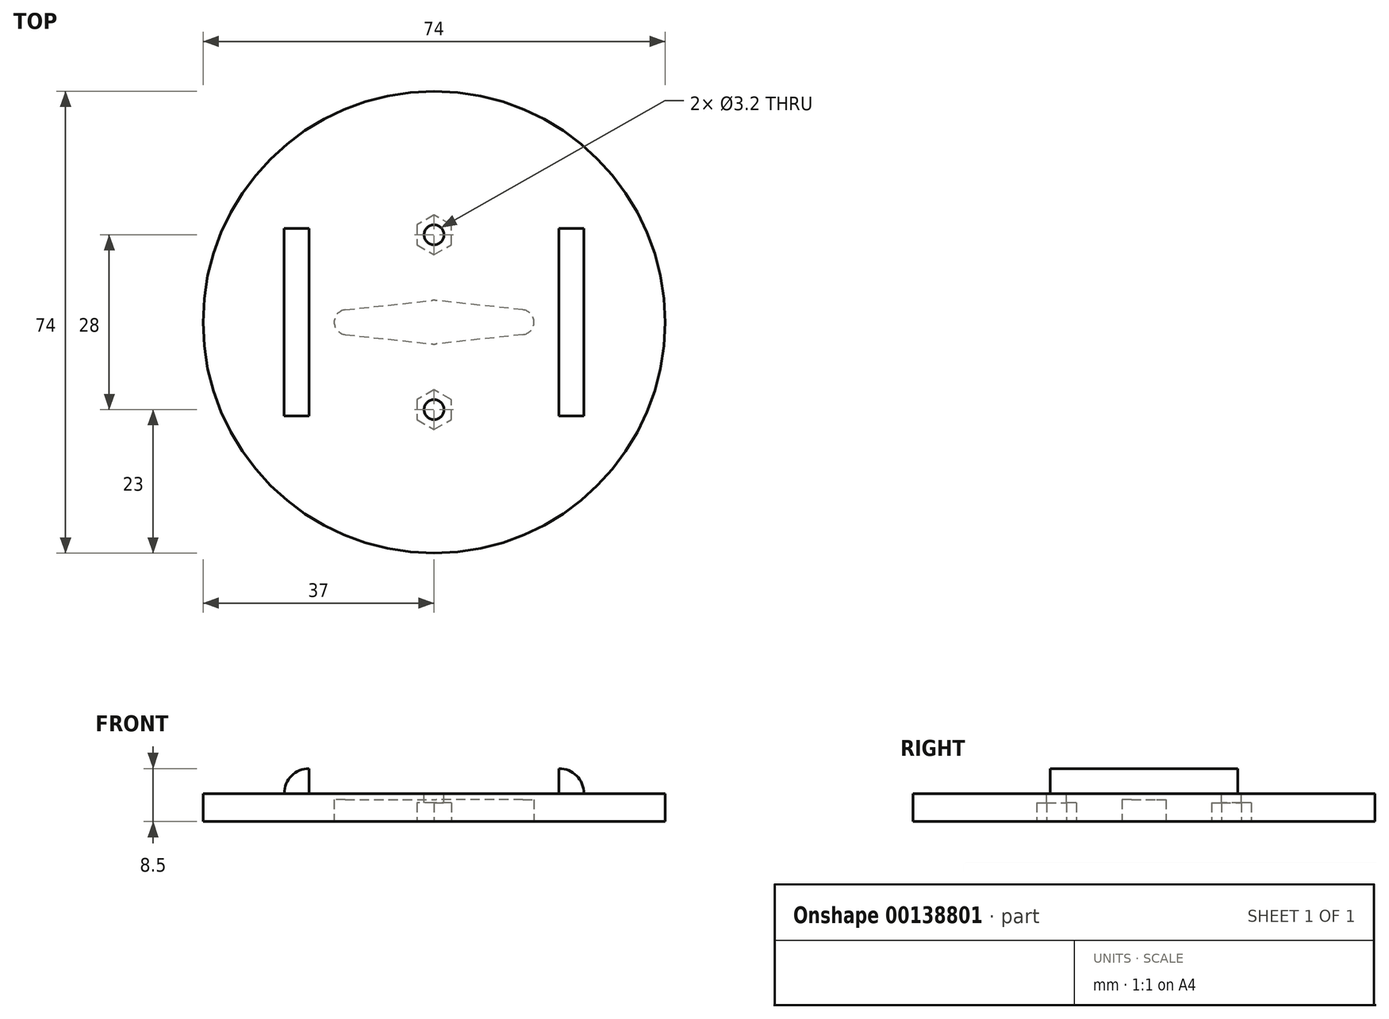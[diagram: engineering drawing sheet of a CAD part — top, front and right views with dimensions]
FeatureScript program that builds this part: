
annotation { "Feature Type Name" : "Feature", "Feature Type Description" : "" }
export const myFeature = defineFeature(function(context is Context, id is Id, definition is map)
    precondition{}
    {
        {
            var Q0;
            Q0=qCreatedBy(makeId("Top.planeOp"),FACE);
            var sketch = newSketch(context, id + "F0", { "sketchPlane" : qUnion([Q0])});
            skCircle(sketch, "E0", {"center": v(0, 0) * mm, "radius": 37 * mm});
            skSolve(sketch);
        }
        {
            var Q0;
            Q0=makeQuery(id+"F0.imprint","IMPRINT",FACE,{"disambiguationData":[TD([[makeQuery(id+"F0.imprint","IMPRINT",EDGE,{"derivedFrom":sQuery(id+"F0.wireOp",EDGE,"E0")}),1.0]])]});
            extrude(context, id + "F1", {"entities" : qUnion([Q0]), "depth" : 4.5 * mm});
        }
        {
            var Q0;
            Q0=makeQuery(id+"F1.opExtrude","CAP_FACE",FACE,{"disambiguationData":[OSD([sQuery(id+"F0.wireOp",EDGE,"E0")])],"isStart":true});
            var sketch = newSketch(context, id + "F2", { "sketchPlane" : qUnion([Q0])});
            skCircle(sketch, "E1", {"center": v(0, 0) * mm, "radius": 3.5 * mm});
            skLineSegment(sketch, "E2", {"start": v(0, 0) * mm, "end": v(0, 14) * mm});
            skCircle(sketch, "E3", {"center": v(0, 14) * mm, "radius": 2 * mm});
            skCircle(sketch, "E4.MirrorC", {"center": v(0, -14) * mm, "radius": 2 * mm});
            skLineSegment(sketch, "E5", {"start": v(-1.99, 14.21) * mm, "end": v(-3.48, 0.38) * mm});
            skLineSegment(sketch, "E6", {"start": v(1.99, 14.21) * mm, "end": v(3.48, 0.37) * mm});
            skLineSegment(sketch, "E7.MirrorCS", {"start": v(-1.99, -14.21) * mm, "end": v(-3.48, -0.38) * mm});
            skLineSegment(sketch, "E8.MirrorCS", {"start": v(1.99, -14.21) * mm, "end": v(3.48, -0.37) * mm});
            skSolve(sketch);
        }
        {
            var Q0;
            Q0=qSketchRegion(id+"F2",true);
            extrude(context, id + "F3", {"entities" : qUnion([Q0]), "operationType" : NewBodyOperationType.REMOVE, "oppositeDirection" : true, "depth" : 3.5 * mm});
        }
        {
            var Q0;
            Q0=qCreatedBy(makeId("Right.planeOp"),FACE);
            var sketch = newSketch(context, id + "F4", { "sketchPlane" : qUnion([Q0])});
            skLineSegment(sketch, "E9.0", {"start": v(-37, 4.5) * mm, "end": v(37, 4.5) * mm});
            skLineSegment(sketch, "E10", {"start": v(20, 4.5) * mm, "end": v(20, 8.5) * mm});
            skArc(sketch, "E11", {"start": v(20, 8.5) * mm, "mid": v(22.83, 7.33) * mm, "end": v(24, 4.5) * mm});
            skLineSegment(sketch, "E12.MirrorCS", {"start": v(-20, 4.5) * mm, "end": v(-20, 8.5) * mm});
            skArc(sketch, "E13.MirrorCS", {"start": v(-20, 8.5) * mm, "mid": v(-22.83, 7.33) * mm, "end": v(-24, 4.5) * mm});
            skSolve(sketch);
        }
        {
            var Q0;
            {var subQ0=sQuery(id+"F4.wireOp",EDGE,"E12.MirrorCS");Q0=makeQuery(id+"F4.imprint","IMPRINT",FACE,{"disambiguationData":[TD([[makeQuery(id+"F4.imprint","IMPRINT",EDGE,{"derivedFrom":subQ0}),1.0]])]});}
            var Q1;
            {var subQ0=sQuery(id+"F4.wireOp",EDGE,"E10");Q1=makeQuery(id+"F4.imprint","IMPRINT",FACE,{"disambiguationData":[TD([[makeQuery(id+"F4.imprint","IMPRINT",EDGE,{"derivedFrom":subQ0}),-1.0]])]});}
            extrude(context, id + "F5", {"entities" : qUnion([Q0, Q1]), "operationType" : NewBodyOperationType.ADD, "endBound" : BoundingType.SYMMETRIC, "depth" : 30 * mm});
        }
        {
            var Q0;
            Q0=makeQuery(id+"F1.opExtrude","CAP_FACE",FACE,{"disambiguationData":[OSD([sQuery(id+"F0.wireOp",EDGE,"E0")])],"isStart":false});
            var sketch = newSketch(context, id + "F6", { "sketchPlane" : qUnion([Q0])});
            skCircle(sketch, "E14", {"center": v(-14, 0) * mm, "radius": 1.6 * mm});
            skCircle(sketch, "E15.MirrorC", {"center": v(14, 0) * mm, "radius": 1.6 * mm});
            skSolve(sketch);
        }
        {
            var Q0;
            Q0=qSketchRegion(id+"F6",true);
            extrude(context, id + "F7", {"entities" : qUnion([Q0]), "operationType" : NewBodyOperationType.REMOVE, "endBound" : BoundingType.THROUGH_ALL, "oppositeDirection" : true, "depth" : 25 * mm});
        }
        {
            var Q0;
            Q0=makeQuery(id+"F1.opExtrude","CAP_FACE",FACE,{"disambiguationData":[OSD([sQuery(id+"F0.wireOp",EDGE,"E0")])],"isStart":true});
            var sketch = newSketch(context, id + "F8", { "sketchPlane" : qUnion([Q0])});
            skCircle(sketch, "E16.cCircle", {"center": v(14, 0) * mm, "radius": 2.75 * mm, "construction": true});
            skLineSegment(sketch, "E16.0", {"start": v(10.82, 0) * mm, "end": v(12.41, 2.75) * mm});
            skLineSegment(sketch, "E16.1", {"start": v(12.41, 2.75) * mm, "end": v(15.59, 2.75) * mm});
            skLineSegment(sketch, "E16.2", {"start": v(15.59, 2.75) * mm, "end": v(17.18, 0) * mm});
            skLineSegment(sketch, "E16.3", {"start": v(17.18, 0) * mm, "end": v(15.59, -2.75) * mm});
            skLineSegment(sketch, "E16.4", {"start": v(15.59, -2.75) * mm, "end": v(12.41, -2.75) * mm});
            skLineSegment(sketch, "E16.5", {"start": v(12.41, -2.75) * mm, "end": v(10.82, 0) * mm});
            skPoint(sketch, "E16.0.midPoint", {"position": v(11.62, 1.38) * mm});
            skLineSegment(sketch, "E17", {"start": v(10.82, 0) * mm, "end": v(17.18, 0) * mm, "construction": true});
            skCircle(sketch, "E18.cCircle", {"center": v(-14, 0) * mm, "radius": 2.75 * mm, "construction": true});
            skLineSegment(sketch, "E18.0", {"start": v(-10.82, 0) * mm, "end": v(-12.41, -2.75) * mm});
            skLineSegment(sketch, "E18.1", {"start": v(-12.41, -2.75) * mm, "end": v(-15.59, -2.75) * mm});
            skLineSegment(sketch, "E18.2", {"start": v(-15.59, -2.75) * mm, "end": v(-17.18, 0) * mm});
            skLineSegment(sketch, "E18.3", {"start": v(-17.18, 0) * mm, "end": v(-15.59, 2.75) * mm});
            skLineSegment(sketch, "E18.4", {"start": v(-15.59, 2.75) * mm, "end": v(-12.41, 2.75) * mm});
            skLineSegment(sketch, "E18.5", {"start": v(-12.41, 2.75) * mm, "end": v(-10.82, 0) * mm});
            skPoint(sketch, "E18.0.midPoint", {"position": v(-11.62, -1.38) * mm});
            skLineSegment(sketch, "E19", {"start": v(-10.82, 0) * mm, "end": v(-17.18, 0) * mm, "construction": true});
            skSolve(sketch);
        }
        {
            var Q0;
            Q0=qSketchRegion(id+"F8",true);
            extrude(context, id + "F9", {"entities" : qUnion([Q0]), "operationType" : NewBodyOperationType.REMOVE, "oppositeDirection" : true, "depth" : 3 * mm});
        }
        {
            var Q0;
            Q0=qCreatedBy(makeId("Right.planeOp"),FACE);
            var sketch = newSketch(context, id + "F10", { "sketchPlane" : qUnion([Q0])});
            skLineSegment(sketch, "E20", {"start": v(0, -3.18) * mm, "end": v(0, 73.83) * mm, "construction": true});
            skSolve(sketch);
        }
        {
            var Q0;
            Q0=makeQuery(id+"F1.opExtrude","SWEPT_BODY",BODY,{"disambiguationData":[OSD([sQuery(id+"F0.wireOp",EDGE,"E0")])]});
            var Q1;
            Q1=sQuery(id+"F10.wireOp",EDGE,"E20");
            var Q2;
            Q2=sQuery(id+"F10.wireOp",EDGE,"E20");
            transform(context, id + "F11", {"entities" : qUnion([Q0]), "transformType" : TransformType.ROTATION, "transformAxis" : qUnion([Q2]), "angle" : 90 * degree, "makeCopy" : false});
        }
    });
